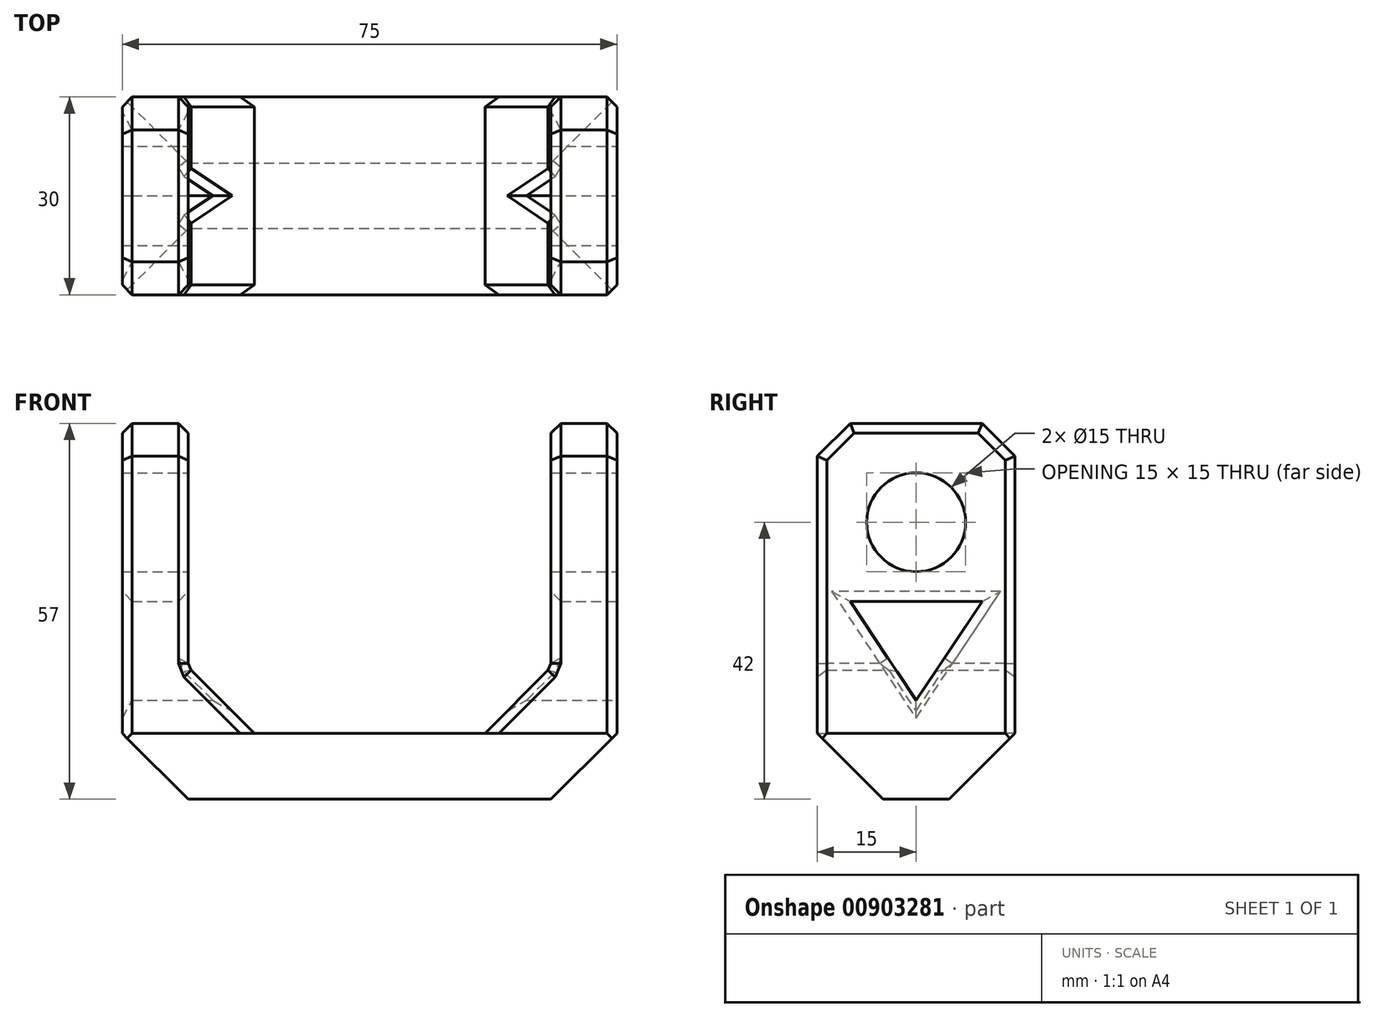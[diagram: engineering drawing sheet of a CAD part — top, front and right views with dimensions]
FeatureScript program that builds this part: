
annotation { "Feature Type Name" : "Feature", "Feature Type Description" : "" }
export const myFeature = defineFeature(function(context is Context, id is Id, definition is map)
    precondition{}
    {
        {
            var Q0;
            Q0=qCreatedBy(makeId("Front.planeOp"),FACE);
            var sketch = newSketch(context, id + "F0", { "sketchPlane" : qUnion([Q0])});
            skLineSegment(sketch, "E0", {"start": v(27.5, 13) * mm, "end": v(27.5, 60) * mm});
            skLineSegment(sketch, "E1", {"start": v(27.5, 60) * mm, "end": v(37.5, 60) * mm});
            skLineSegment(sketch, "E2", {"start": v(37.5, 60) * mm, "end": v(37.5, 3) * mm});
            skLineSegment(sketch, "E3", {"start": v(37.5, 3) * mm, "end": v(-37.5, 3) * mm});
            skLineSegment(sketch, "E4", {"start": v(-37.5, 3) * mm, "end": v(-37.5, 60) * mm});
            skLineSegment(sketch, "E5", {"start": v(-37.5, 60) * mm, "end": v(-27.5, 60) * mm});
            skLineSegment(sketch, "E6", {"start": v(-27.5, 60) * mm, "end": v(-27.5, 13) * mm});
            skLineSegment(sketch, "E7", {"start": v(27.5, 13) * mm, "end": v(-27.5, 13) * mm});
            skPoint(sketch, "E8", {"position": v(0, 0) * mm});
            skLineSegment(sketch, "E9", {"start": v(5.05, 3.56) * mm, "end": v(5.05, 3.56) * mm});
            skPoint(sketch, "E10", {"position": v(-27.5, 13) * mm});
            skLineSegment(sketch, "E11", {"start": v(0, 0) * mm, "end": v(0, 0) * mm});
            skLineSegment(sketch, "E12", {"start": v(0, 0) * mm, "end": v(0, 3) * mm, "construction": true});
            skPoint(sketch, "E12.endSnap0", {"position": v(0, 3) * mm});
            skSolve(sketch);
        }
        {
            var Q0;
            Q0=makeQuery(id+"F0.imprint","IMPRINT",FACE,{"disambiguationData":[TD([[makeQuery(id+"F0.imprint","IMPRINT",EDGE,{"derivedFrom":sQuery(id+"F0.wireOp",EDGE,"E0")}),-1.0]])]});
            extrude(context, id + "F1", {"entities" : qUnion([Q0]), "depth" : 30 * mm, "offsetDistance" : 25 * mm, "symmetric" : true});
        }
        {
            var Q0;
            Q0=makeQuery(id+"F1.opExtrude","SWEPT_FACE",FACE,{"disambiguationData":[OSD([sQuery(id+"F0.wireOp",EDGE,"E2")])]});
            var sketch = newSketch(context, id + "F2", { "sketchPlane" : qUnion([Q0])});
            skCircle(sketch, "E13", {"center": v(0, 45) * mm, "radius": 7.5 * mm});
            skLineSegment(sketch, "E14", {"start": v(0, 0) * mm, "end": v(0, 45) * mm, "construction": true});
            skSolve(sketch);
        }
        {
            var Q0;
            Q0=makeQuery(id+"F2.imprint","IMPRINT",FACE,{"disambiguationData":[TD([[makeQuery(id+"F2.imprint","IMPRINT",EDGE,{"derivedFrom":sQuery(id+"F2.wireOp",EDGE,"E13")}),1.0]])]});
            var Q1;
            Q1=sQuery(id+"F2.wireOp",EDGE,"E13");
            extrude(context, id + "F3", {"entities" : qUnion([Q0]), "operationType" : NewBodyOperationType.REMOVE, "surfaceEntities" : qUnion([Q1]), "endBound" : BoundingType.THROUGH_ALL, "oppositeDirection" : true, "depth" : 25 * mm, "offsetDistance" : 25 * mm});
        }
        {
            var Q0;
            Q0=makeQuery(id+"F1.opExtrude","SWEPT_EDGE",EDGE,{"disambiguationData":[OSD([sQuery(id+"F0.wireOp",EDGE,"E2"),sQuery(id+"F0.wireOp",EDGE,"E3")])]});
            var Q1;
            Q1=makeQuery(id+"F1.opExtrude","SWEPT_EDGE",EDGE,{"disambiguationData":[OSD([sQuery(id+"F0.wireOp",EDGE,"E3"),sQuery(id+"F0.wireOp",EDGE,"E4")])]});
            var Q2;
            Q2=makeQuery(id+"F1.opExtrude","SWEPT_EDGE",EDGE,{"disambiguationData":[OSD([sQuery(id+"F0.wireOp",EDGE,"E6"),sQuery(id+"F0.wireOp",EDGE,"E7")])]});
            var Q3;
            Q3=makeQuery(id+"F1.opExtrude","SWEPT_EDGE",EDGE,{"disambiguationData":[OSD([sQuery(id+"F0.wireOp",EDGE,"E0"),sQuery(id+"F0.wireOp",EDGE,"E7")])]});
            chamfer(context, id + "F4", {"entities" : qUnion([Q0, Q1, Q2, Q3]), "width" : 10 * mm, "tangentPropagation" : true});
        }
        {
            var Q0;
            Q0=makeQuery(id+"F1.opExtrude","CAP_EDGE",EDGE,{"disambiguationData":[OSD([sQuery(id+"F0.wireOp",EDGE,"E3")])],"isStart":false});
            var Q1;
            Q1=makeQuery(id+"F1.opExtrude","CAP_EDGE",EDGE,{"disambiguationData":[OSD([sQuery(id+"F0.wireOp",EDGE,"E3")])],"isStart":true});
            chamfer(context, id + "F5", {"entities" : qUnion([Q0, Q1]), "width" : 10 * mm, "tangentPropagation" : true});
        }
        {
            var Q0;
            Q0=makeQuery(id+"F1.opExtrude","CAP_EDGE",EDGE,{"disambiguationData":[OSD([sQuery(id+"F0.wireOp",EDGE,"E5")])],"isStart":false});
            var Q1;
            Q1=makeQuery(id+"F1.opExtrude","CAP_EDGE",EDGE,{"disambiguationData":[OSD([sQuery(id+"F0.wireOp",EDGE,"E5")])],"isStart":true});
            var Q2;
            Q2=makeQuery(id+"F1.opExtrude","CAP_EDGE",EDGE,{"disambiguationData":[OSD([sQuery(id+"F0.wireOp",EDGE,"E1")])],"isStart":true});
            var Q3;
            Q3=makeQuery(id+"F1.opExtrude","CAP_EDGE",EDGE,{"disambiguationData":[OSD([sQuery(id+"F0.wireOp",EDGE,"E1")])],"isStart":false});
            chamfer(context, id + "F6", {"entities" : qUnion([Q0, Q1, Q2, Q3]), "width" : 5 * mm, "tangentPropagation" : true});
        }
        {
            var Q0;
            Q0=makeQuery(id+"F2.imprint","IMPRINT",FACE,{"disambiguationData":[TD([[makeQuery(id+"F2.imprint","IMPRINT",EDGE,{"derivedFrom":sQuery(id+"F2.wireOp",EDGE,"E13")}),-1.0]])]});
            var sketch = newSketch(context, id + "F7", { "sketchPlane" : qUnion([Q0])});
            skLineSegment(sketch, "E15", {"start": v(0, 18) * mm, "end": v(-10, 33) * mm});
            skLineSegment(sketch, "E16", {"start": v(-10, 33) * mm, "end": v(10, 33) * mm});
            skLineSegment(sketch, "E17", {"start": v(10, 33) * mm, "end": v(0, 18) * mm});
            skSolve(sketch);
        }
        {
            var Q0;
            Q0=makeQuery(id+"F7.imprint","IMPRINT",FACE,{"disambiguationData":[TD([[makeQuery(id+"F7.imprint","IMPRINT",EDGE,{"derivedFrom":sQuery(id+"F7.wireOp",EDGE,"E15")}),-1.0]])]});
            extrude(context, id + "F8", {"entities" : qUnion([Q0]), "operationType" : NewBodyOperationType.REMOVE, "endBound" : BoundingType.THROUGH_ALL, "oppositeDirection" : true, "depth" : 25 * mm, "offsetDistance" : 25 * mm});
        }
        {
            var Q0;
            Q0=makeQuery(id+"F1.opExtrude","CAP_EDGE",EDGE,{"disambiguationData":[OSD([sQuery(id+"F0.wireOp",EDGE,"E2")])],"isStart":false});
            var Q1;
            Q1=makeQuery(id+"F8.boolean.opBoolean","COPY",EDGE,{"derivedFrom":makeQuery(id+"F8.opExtrude","CAP_EDGE",EDGE,{"disambiguationData":[OSD([sQuery(id+"F7.wireOp",EDGE,"E15")])],"isStart":true})});
            var Q2;
            Q2=makeQuery(id+"F8.boolean.opBoolean","COPY",EDGE,{"derivedFrom":makeQuery(id+"F8.opExtrude","CAP_EDGE",EDGE,{"disambiguationData":[OSD([sQuery(id+"F7.wireOp",EDGE,"E16")])],"isStart":true})});
            var Q3;
            Q3=makeQuery(id+"F8.boolean.opBoolean","COPY",EDGE,{"derivedFrom":makeQuery(id+"F8.opExtrude","CAP_EDGE",EDGE,{"disambiguationData":[OSD([sQuery(id+"F7.wireOp",EDGE,"E17")])],"isStart":true})});
            var Q4;
            Q4=makeQuery(id+"F1.opExtrude","CAP_EDGE",EDGE,{"disambiguationData":[OSD([sQuery(id+"F0.wireOp",EDGE,"E2")])],"isStart":true});
            var Q5;
            Q5=makeQuery(id+"F1.opExtrude","SWEPT_EDGE",EDGE,{"disambiguationData":[OSD([sQuery(id+"F0.wireOp",EDGE,"E0"),sQuery(id+"F0.wireOp",EDGE,"E1")])]});
            var Q6;
            Q6=makeQuery(id+"F1.opExtrude","SWEPT_EDGE",EDGE,{"disambiguationData":[OSD([sQuery(id+"F0.wireOp",EDGE,"E1"),sQuery(id+"F0.wireOp",EDGE,"E2")])]});
            var Q7;
            Q7=makeQuery(id+"F6.opChamfer","BLEND_EDGE",EDGE,{"blendedFrom":[makeQuery(id+"F1.opExtrude","CAP_EDGE",EDGE,{"disambiguationData":[OSD([sQuery(id+"F0.wireOp",EDGE,"E1")])],"isStart":false}),makeQuery(id+"F1.opExtrude","SWEPT_FACE",FACE,{"disambiguationData":[OSD([sQuery(id+"F0.wireOp",EDGE,"E2")])]})],"blendedInto":[makeQuery(id+"F1.opExtrude","SWEPT_FACE",FACE,{"disambiguationData":[OSD([sQuery(id+"F0.wireOp",EDGE,"E2")])]})]});
            var Q8;
            Q8=makeQuery(id+"F6.opChamfer","BLEND_EDGE",EDGE,{"blendedFrom":[makeQuery(id+"F1.opExtrude","CAP_EDGE",EDGE,{"disambiguationData":[OSD([sQuery(id+"F0.wireOp",EDGE,"E1")])],"isStart":true}),makeQuery(id+"F1.opExtrude","SWEPT_FACE",FACE,{"disambiguationData":[OSD([sQuery(id+"F0.wireOp",EDGE,"E2")])]})],"blendedInto":[makeQuery(id+"F1.opExtrude","SWEPT_FACE",FACE,{"disambiguationData":[OSD([sQuery(id+"F0.wireOp",EDGE,"E2")])]})]});
            var Q9;
            Q9=makeQuery(id+"F1.opExtrude","CAP_EDGE",EDGE,{"disambiguationData":[OSD([sQuery(id+"F0.wireOp",EDGE,"E0")])],"isStart":false});
            var Q10;
            Q10=makeQuery(id+"F6.opChamfer","BLEND_EDGE",EDGE,{"blendedFrom":[makeQuery(id+"F1.opExtrude","CAP_EDGE",EDGE,{"disambiguationData":[OSD([sQuery(id+"F0.wireOp",EDGE,"E1")])],"isStart":false}),makeQuery(id+"F1.opExtrude","SWEPT_FACE",FACE,{"disambiguationData":[OSD([sQuery(id+"F0.wireOp",EDGE,"E0")])]})],"blendedInto":[makeQuery(id+"F1.opExtrude","SWEPT_FACE",FACE,{"disambiguationData":[OSD([sQuery(id+"F0.wireOp",EDGE,"E0")])]})]});
            var Q11;
            Q11=makeQuery(id+"F6.opChamfer","BLEND_EDGE",EDGE,{"blendedFrom":[makeQuery(id+"F1.opExtrude","CAP_EDGE",EDGE,{"disambiguationData":[OSD([sQuery(id+"F0.wireOp",EDGE,"E1")])],"isStart":true}),makeQuery(id+"F1.opExtrude","SWEPT_FACE",FACE,{"disambiguationData":[OSD([sQuery(id+"F0.wireOp",EDGE,"E0")])]})],"blendedInto":[makeQuery(id+"F1.opExtrude","SWEPT_FACE",FACE,{"disambiguationData":[OSD([sQuery(id+"F0.wireOp",EDGE,"E0")])]})]});
            var Q12;
            Q12=makeQuery(id+"F1.opExtrude","CAP_EDGE",EDGE,{"disambiguationData":[OSD([sQuery(id+"F0.wireOp",EDGE,"E0")])],"isStart":true});
            var Q13;
            {var subQ0=sQuery(id+"F0.wireOp",EDGE,"E7");var subQ1=sQuery(id+"F0.wireOp",EDGE,"E0");Q13=makeQuery(id+"F4.opChamfer","BLEND_EDGE",EDGE,{"blendedFrom":[makeQuery(id+"F1.opExtrude","SWEPT_EDGE",EDGE,{"disambiguationData":[OSD([subQ1,subQ0])]}),makeQuery(id+"F1.opExtrude","CAP_FACE",FACE,{"disambiguationData":[OSD([subQ1,sQuery(id+"F0.wireOp",EDGE,"E1"),sQuery(id+"F0.wireOp",EDGE,"E2"),sQuery(id+"F0.wireOp",EDGE,"E3"),sQuery(id+"F0.wireOp",EDGE,"E4"),sQuery(id+"F0.wireOp",EDGE,"E5"),sQuery(id+"F0.wireOp",EDGE,"E6"),subQ0])],"isStart":true})],"blendedInto":[makeQuery(id+"F1.opExtrude","CAP_FACE",FACE,{"disambiguationData":[OSD([subQ1,sQuery(id+"F0.wireOp",EDGE,"E1"),sQuery(id+"F0.wireOp",EDGE,"E2"),sQuery(id+"F0.wireOp",EDGE,"E3"),sQuery(id+"F0.wireOp",EDGE,"E4"),sQuery(id+"F0.wireOp",EDGE,"E5"),sQuery(id+"F0.wireOp",EDGE,"E6"),subQ0])],"isStart":true})]});}
            var Q14;
            Q14=makeQuery(id+"F8.boolean.opBoolean","INTERSECT",EDGE,{"derivedFrom":[makeQuery(id+"F1.opExtrude","SWEPT_FACE",FACE,{"disambiguationData":[OSD([sQuery(id+"F0.wireOp",EDGE,"E0")])]}),makeQuery(id+"F8.opExtrude","SWEPT_FACE",FACE,{"disambiguationData":[OSD([sQuery(id+"F7.wireOp",EDGE,"E16")])]})]});
            var Q15;
            Q15=makeQuery(id+"F8.boolean.opBoolean","INTERSECT",EDGE,{"derivedFrom":[makeQuery(id+"F1.opExtrude","SWEPT_FACE",FACE,{"disambiguationData":[OSD([sQuery(id+"F0.wireOp",EDGE,"E0")])]}),makeQuery(id+"F8.opExtrude","SWEPT_FACE",FACE,{"disambiguationData":[OSD([sQuery(id+"F7.wireOp",EDGE,"E17")])]})]});
            var Q16;
            Q16=makeQuery(id+"F8.boolean.opBoolean","INTERSECT",EDGE,{"derivedFrom":[makeQuery(id+"F1.opExtrude","SWEPT_FACE",FACE,{"disambiguationData":[OSD([sQuery(id+"F0.wireOp",EDGE,"E0")])]}),makeQuery(id+"F8.opExtrude","SWEPT_FACE",FACE,{"disambiguationData":[OSD([sQuery(id+"F7.wireOp",EDGE,"E15")])]})]});
            var Q17;
            Q17=makeQuery(id+"F8.boolean.opBoolean","INTERSECT",EDGE,{"derivedFrom":[makeQuery(id+"F4.opChamfer","BLEND_FACE",FACE,{"disambiguationData":[OSD([sQuery(id+"F0.wireOp",EDGE,"E0"),sQuery(id+"F0.wireOp",EDGE,"E7")])]}),makeQuery(id+"F8.opExtrude","SWEPT_FACE",FACE,{"disambiguationData":[OSD([sQuery(id+"F7.wireOp",EDGE,"E15")])]})]});
            var Q18;
            Q18=makeQuery(id+"F8.boolean.opBoolean","INTERSECT",EDGE,{"derivedFrom":[makeQuery(id+"F4.opChamfer","BLEND_FACE",FACE,{"disambiguationData":[OSD([sQuery(id+"F0.wireOp",EDGE,"E0"),sQuery(id+"F0.wireOp",EDGE,"E7")])]}),makeQuery(id+"F8.opExtrude","SWEPT_FACE",FACE,{"disambiguationData":[OSD([sQuery(id+"F7.wireOp",EDGE,"E17")])]})]});
            var Q19;
            {var subQ0=sQuery(id+"F0.wireOp",EDGE,"E0");var subQ1=makeQuery(id+"F1.opExtrude","SWEPT_FACE",FACE,{"disambiguationData":[OSD([subQ0])]});var subQ2=sQuery(id+"F0.wireOp",EDGE,"E7");Q19=makeQuery(id+"F8.boolean.opBoolean","SPLIT",EDGE,{"disambiguationData":[TD([makeQuery(id+"F8.opExtrude","SWEPT_FACE",FACE,{"disambiguationData":[OSD([sQuery(id+"F7.wireOp",EDGE,"E17")])]})])],"derivedFrom":makeQuery(id+"F4.opChamfer","BLEND_EDGE",EDGE,{"blendedFrom":[makeQuery(id+"F1.opExtrude","SWEPT_EDGE",EDGE,{"disambiguationData":[OSD([subQ0,subQ2])]}),subQ1],"blendedInto":[subQ1]})});}
            var Q20;
            {var subQ0=sQuery(id+"F0.wireOp",EDGE,"E0");var subQ1=makeQuery(id+"F1.opExtrude","SWEPT_FACE",FACE,{"disambiguationData":[OSD([subQ0])]});var subQ2=sQuery(id+"F0.wireOp",EDGE,"E7");Q20=makeQuery(id+"F8.boolean.opBoolean","SPLIT",EDGE,{"disambiguationData":[TD([makeQuery(id+"F8.opExtrude","SWEPT_FACE",FACE,{"disambiguationData":[OSD([sQuery(id+"F7.wireOp",EDGE,"E15")])]})])],"derivedFrom":makeQuery(id+"F4.opChamfer","BLEND_EDGE",EDGE,{"blendedFrom":[makeQuery(id+"F1.opExtrude","SWEPT_EDGE",EDGE,{"disambiguationData":[OSD([subQ0,subQ2])]}),subQ1],"blendedInto":[subQ1]})});}
            var Q21;
            Q21=makeQuery(id+"F1.opExtrude","CAP_EDGE",EDGE,{"disambiguationData":[OSD([sQuery(id+"F0.wireOp",EDGE,"E6")])],"isStart":true});
            var Q22;
            Q22=makeQuery(id+"F1.opExtrude","CAP_EDGE",EDGE,{"disambiguationData":[OSD([sQuery(id+"F0.wireOp",EDGE,"E4")])],"isStart":true});
            var Q23;
            Q23=makeQuery(id+"F6.opChamfer","BLEND_EDGE",EDGE,{"blendedFrom":[makeQuery(id+"F1.opExtrude","CAP_EDGE",EDGE,{"disambiguationData":[OSD([sQuery(id+"F0.wireOp",EDGE,"E5")])],"isStart":true}),makeQuery(id+"F1.opExtrude","SWEPT_FACE",FACE,{"disambiguationData":[OSD([sQuery(id+"F0.wireOp",EDGE,"E6")])]})],"blendedInto":[makeQuery(id+"F1.opExtrude","SWEPT_FACE",FACE,{"disambiguationData":[OSD([sQuery(id+"F0.wireOp",EDGE,"E6")])]})]});
            var Q24;
            Q24=makeQuery(id+"F1.opExtrude","SWEPT_EDGE",EDGE,{"disambiguationData":[OSD([sQuery(id+"F0.wireOp",EDGE,"E5"),sQuery(id+"F0.wireOp",EDGE,"E6")])]});
            var Q25;
            Q25=makeQuery(id+"F1.opExtrude","SWEPT_EDGE",EDGE,{"disambiguationData":[OSD([sQuery(id+"F0.wireOp",EDGE,"E4"),sQuery(id+"F0.wireOp",EDGE,"E5")])]});
            var Q26;
            Q26=makeQuery(id+"F6.opChamfer","BLEND_EDGE",EDGE,{"blendedFrom":[makeQuery(id+"F1.opExtrude","CAP_EDGE",EDGE,{"disambiguationData":[OSD([sQuery(id+"F0.wireOp",EDGE,"E5")])],"isStart":true}),makeQuery(id+"F1.opExtrude","SWEPT_FACE",FACE,{"disambiguationData":[OSD([sQuery(id+"F0.wireOp",EDGE,"E4")])]})],"blendedInto":[makeQuery(id+"F1.opExtrude","SWEPT_FACE",FACE,{"disambiguationData":[OSD([sQuery(id+"F0.wireOp",EDGE,"E4")])]})]});
            var Q27;
            Q27=makeQuery(id+"F8.boolean.opBoolean","INTERSECT",EDGE,{"derivedFrom":[makeQuery(id+"F1.opExtrude","SWEPT_FACE",FACE,{"disambiguationData":[OSD([sQuery(id+"F0.wireOp",EDGE,"E4")])]}),makeQuery(id+"F8.opExtrude","SWEPT_FACE",FACE,{"disambiguationData":[OSD([sQuery(id+"F7.wireOp",EDGE,"E17")])]})]});
            var Q28;
            Q28=makeQuery(id+"F8.boolean.opBoolean","INTERSECT",EDGE,{"derivedFrom":[makeQuery(id+"F1.opExtrude","SWEPT_FACE",FACE,{"disambiguationData":[OSD([sQuery(id+"F0.wireOp",EDGE,"E4")])]}),makeQuery(id+"F8.opExtrude","SWEPT_FACE",FACE,{"disambiguationData":[OSD([sQuery(id+"F7.wireOp",EDGE,"E16")])]})]});
            var Q29;
            Q29=makeQuery(id+"F8.boolean.opBoolean","INTERSECT",EDGE,{"derivedFrom":[makeQuery(id+"F1.opExtrude","SWEPT_FACE",FACE,{"disambiguationData":[OSD([sQuery(id+"F0.wireOp",EDGE,"E4")])]}),makeQuery(id+"F8.opExtrude","SWEPT_FACE",FACE,{"disambiguationData":[OSD([sQuery(id+"F7.wireOp",EDGE,"E15")])]})]});
            var Q30;
            Q30=makeQuery(id+"F8.boolean.opBoolean","INTERSECT",EDGE,{"derivedFrom":[makeQuery(id+"F1.opExtrude","SWEPT_FACE",FACE,{"disambiguationData":[OSD([sQuery(id+"F0.wireOp",EDGE,"E6")])]}),makeQuery(id+"F8.opExtrude","SWEPT_FACE",FACE,{"disambiguationData":[OSD([sQuery(id+"F7.wireOp",EDGE,"E15")])]})]});
            var Q31;
            Q31=makeQuery(id+"F8.boolean.opBoolean","INTERSECT",EDGE,{"derivedFrom":[makeQuery(id+"F4.opChamfer","BLEND_FACE",FACE,{"disambiguationData":[OSD([sQuery(id+"F0.wireOp",EDGE,"E6"),sQuery(id+"F0.wireOp",EDGE,"E7")])]}),makeQuery(id+"F8.opExtrude","SWEPT_FACE",FACE,{"disambiguationData":[OSD([sQuery(id+"F7.wireOp",EDGE,"E15")])]})]});
            var Q32;
            Q32=makeQuery(id+"F8.boolean.opBoolean","INTERSECT",EDGE,{"derivedFrom":[makeQuery(id+"F4.opChamfer","BLEND_FACE",FACE,{"disambiguationData":[OSD([sQuery(id+"F0.wireOp",EDGE,"E6"),sQuery(id+"F0.wireOp",EDGE,"E7")])]}),makeQuery(id+"F8.opExtrude","SWEPT_FACE",FACE,{"disambiguationData":[OSD([sQuery(id+"F7.wireOp",EDGE,"E17")])]})]});
            var Q33;
            Q33=makeQuery(id+"F8.boolean.opBoolean","INTERSECT",EDGE,{"derivedFrom":[makeQuery(id+"F1.opExtrude","SWEPT_FACE",FACE,{"disambiguationData":[OSD([sQuery(id+"F0.wireOp",EDGE,"E6")])]}),makeQuery(id+"F8.opExtrude","SWEPT_FACE",FACE,{"disambiguationData":[OSD([sQuery(id+"F7.wireOp",EDGE,"E17")])]})]});
            var Q34;
            Q34=makeQuery(id+"F8.boolean.opBoolean","INTERSECT",EDGE,{"derivedFrom":[makeQuery(id+"F1.opExtrude","SWEPT_FACE",FACE,{"disambiguationData":[OSD([sQuery(id+"F0.wireOp",EDGE,"E6")])]}),makeQuery(id+"F8.opExtrude","SWEPT_FACE",FACE,{"disambiguationData":[OSD([sQuery(id+"F7.wireOp",EDGE,"E16")])]})]});
            var Q35;
            Q35=makeQuery(id+"F1.opExtrude","CAP_EDGE",EDGE,{"disambiguationData":[OSD([sQuery(id+"F0.wireOp",EDGE,"E6")])],"isStart":false});
            var Q36;
            Q36=makeQuery(id+"F6.opChamfer","BLEND_EDGE",EDGE,{"blendedFrom":[makeQuery(id+"F1.opExtrude","CAP_EDGE",EDGE,{"disambiguationData":[OSD([sQuery(id+"F0.wireOp",EDGE,"E5")])],"isStart":false}),makeQuery(id+"F1.opExtrude","SWEPT_FACE",FACE,{"disambiguationData":[OSD([sQuery(id+"F0.wireOp",EDGE,"E6")])]})],"blendedInto":[makeQuery(id+"F1.opExtrude","SWEPT_FACE",FACE,{"disambiguationData":[OSD([sQuery(id+"F0.wireOp",EDGE,"E6")])]})]});
            var Q37;
            {var subQ0=sQuery(id+"F0.wireOp",EDGE,"E7");var subQ1=sQuery(id+"F0.wireOp",EDGE,"E6");Q37=makeQuery(id+"F4.opChamfer","BLEND_EDGE",EDGE,{"blendedFrom":[makeQuery(id+"F1.opExtrude","SWEPT_EDGE",EDGE,{"disambiguationData":[OSD([subQ1,subQ0])]}),makeQuery(id+"F1.opExtrude","CAP_FACE",FACE,{"disambiguationData":[OSD([sQuery(id+"F0.wireOp",EDGE,"E0"),sQuery(id+"F0.wireOp",EDGE,"E1"),sQuery(id+"F0.wireOp",EDGE,"E2"),sQuery(id+"F0.wireOp",EDGE,"E3"),sQuery(id+"F0.wireOp",EDGE,"E4"),sQuery(id+"F0.wireOp",EDGE,"E5"),subQ1,subQ0])],"isStart":false})],"blendedInto":[makeQuery(id+"F1.opExtrude","CAP_FACE",FACE,{"disambiguationData":[OSD([sQuery(id+"F0.wireOp",EDGE,"E0"),sQuery(id+"F0.wireOp",EDGE,"E1"),sQuery(id+"F0.wireOp",EDGE,"E2"),sQuery(id+"F0.wireOp",EDGE,"E3"),sQuery(id+"F0.wireOp",EDGE,"E4"),sQuery(id+"F0.wireOp",EDGE,"E5"),subQ1,subQ0])],"isStart":false})]});}
            var Q38;
            Q38=makeQuery(id+"F6.opChamfer","BLEND_EDGE",EDGE,{"blendedFrom":[makeQuery(id+"F1.opExtrude","CAP_EDGE",EDGE,{"disambiguationData":[OSD([sQuery(id+"F0.wireOp",EDGE,"E5")])],"isStart":false}),makeQuery(id+"F1.opExtrude","SWEPT_FACE",FACE,{"disambiguationData":[OSD([sQuery(id+"F0.wireOp",EDGE,"E4")])]})],"blendedInto":[makeQuery(id+"F1.opExtrude","SWEPT_FACE",FACE,{"disambiguationData":[OSD([sQuery(id+"F0.wireOp",EDGE,"E4")])]})]});
            var Q39;
            Q39=makeQuery(id+"F1.opExtrude","CAP_EDGE",EDGE,{"disambiguationData":[OSD([sQuery(id+"F0.wireOp",EDGE,"E4")])],"isStart":false});
            var Q40;
            {var subQ0=sQuery(id+"F0.wireOp",EDGE,"E7");var subQ1=sQuery(id+"F0.wireOp",EDGE,"E6");Q40=makeQuery(id+"F4.opChamfer","BLEND_EDGE",EDGE,{"blendedFrom":[makeQuery(id+"F1.opExtrude","SWEPT_EDGE",EDGE,{"disambiguationData":[OSD([subQ1,subQ0])]}),makeQuery(id+"F1.opExtrude","CAP_FACE",FACE,{"disambiguationData":[OSD([sQuery(id+"F0.wireOp",EDGE,"E0"),sQuery(id+"F0.wireOp",EDGE,"E1"),sQuery(id+"F0.wireOp",EDGE,"E2"),sQuery(id+"F0.wireOp",EDGE,"E3"),sQuery(id+"F0.wireOp",EDGE,"E4"),sQuery(id+"F0.wireOp",EDGE,"E5"),subQ1,subQ0])],"isStart":true})],"blendedInto":[makeQuery(id+"F1.opExtrude","CAP_FACE",FACE,{"disambiguationData":[OSD([sQuery(id+"F0.wireOp",EDGE,"E0"),sQuery(id+"F0.wireOp",EDGE,"E1"),sQuery(id+"F0.wireOp",EDGE,"E2"),sQuery(id+"F0.wireOp",EDGE,"E3"),sQuery(id+"F0.wireOp",EDGE,"E4"),sQuery(id+"F0.wireOp",EDGE,"E5"),subQ1,subQ0])],"isStart":true})]});}
            var Q41;
            {var subQ0=sQuery(id+"F0.wireOp",EDGE,"E7");var subQ1=sQuery(id+"F0.wireOp",EDGE,"E6");var subQ2=makeQuery(id+"F1.opExtrude","SWEPT_FACE",FACE,{"disambiguationData":[OSD([subQ1])]});Q41=makeQuery(id+"F8.boolean.opBoolean","SPLIT",EDGE,{"disambiguationData":[TD([makeQuery(id+"F8.opExtrude","SWEPT_FACE",FACE,{"disambiguationData":[OSD([sQuery(id+"F7.wireOp",EDGE,"E17")])]})])],"derivedFrom":makeQuery(id+"F4.opChamfer","BLEND_EDGE",EDGE,{"blendedFrom":[makeQuery(id+"F1.opExtrude","SWEPT_EDGE",EDGE,{"disambiguationData":[OSD([subQ1,subQ0])]}),subQ2],"blendedInto":[subQ2]})});}
            var Q42;
            {var subQ0=sQuery(id+"F0.wireOp",EDGE,"E7");var subQ1=sQuery(id+"F0.wireOp",EDGE,"E6");var subQ2=makeQuery(id+"F1.opExtrude","SWEPT_FACE",FACE,{"disambiguationData":[OSD([subQ1])]});Q42=makeQuery(id+"F8.boolean.opBoolean","SPLIT",EDGE,{"disambiguationData":[TD([makeQuery(id+"F8.opExtrude","SWEPT_FACE",FACE,{"disambiguationData":[OSD([sQuery(id+"F7.wireOp",EDGE,"E15")])]})])],"derivedFrom":makeQuery(id+"F4.opChamfer","BLEND_EDGE",EDGE,{"blendedFrom":[makeQuery(id+"F1.opExtrude","SWEPT_EDGE",EDGE,{"disambiguationData":[OSD([subQ1,subQ0])]}),subQ2],"blendedInto":[subQ2]})});}
            chamfer(context, id + "F9", {"entities" : qUnion([Q0, Q1, Q2, Q3, Q4, Q5, Q6, Q7, Q8, Q9, Q10, Q11, Q12, Q13, Q14, Q15, Q16, Q17, Q18, Q19, Q20, Q21, Q22, Q23, Q24, Q25, Q26, Q27, Q28, Q29, Q30, Q31, Q32, Q33, Q34, Q35, Q36, Q37, Q38, Q39, Q40, Q41, Q42]), "width" : 1.5 * mm, "tangentPropagation" : true});
        }
    });
